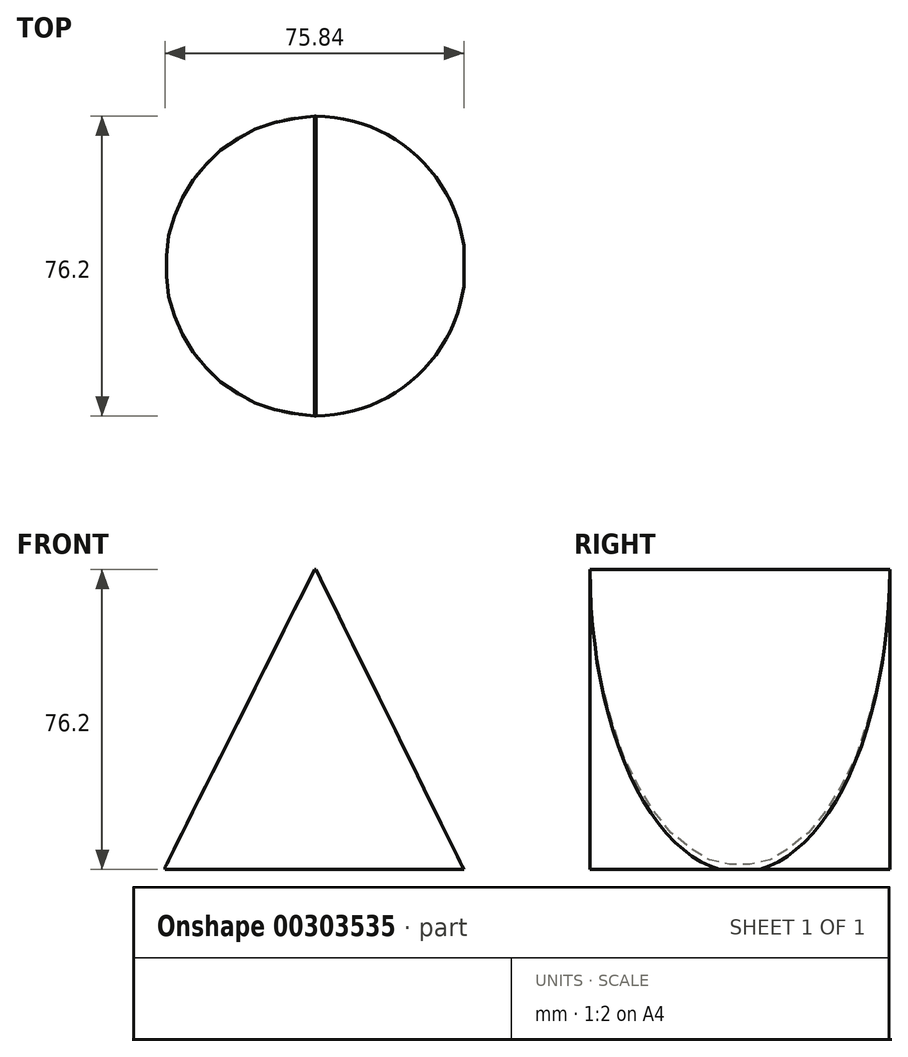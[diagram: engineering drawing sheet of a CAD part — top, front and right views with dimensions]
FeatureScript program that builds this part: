
annotation { "Feature Type Name" : "Feature", "Feature Type Description" : "" }
export const myFeature = defineFeature(function(context is Context, id is Id, definition is map)
    precondition{}
    {
        {
            var Q0;
            Q0=qCreatedBy(makeId("Top.planeOp"),FACE);
            var sketch = newSketch(context, id + "F0", { "sketchPlane" : qUnion([Q0])});
            skCircle(sketch, "E0", {"center": v(0, 0) * mm, "radius": 38.1 * mm});
            skSolve(sketch);
        }
        {
            var Q0;
            Q0 = qSketchRegion(id + "F0", true);
            extrude(context, id + "F1", {"entities" : qUnion([Q0]), "depth" : 76.2 * mm});
        }
        {
            var Q0;
            Q0=qCreatedBy(makeId("Front.planeOp"),FACE);
            var sketch = newSketch(context, id + "F2", { "sketchPlane" : qUnion([Q0])});
            skLineSegment(sketch, "E1", {"start": v(-38.44, 0) * mm, "end": v(0, 76.53) * mm});
            skLineSegment(sketch, "E2", {"start": v(0, 76.53) * mm, "end": v(37.74, 0) * mm});
            skLineSegment(sketch, "E3", {"start": v(37.74, 0) * mm, "end": v(45.74, 0) * mm});
            skLineSegment(sketch, "E4", {"start": v(45.74, 0) * mm, "end": v(45.74, 81.06) * mm});
            skLineSegment(sketch, "E5", {"start": v(45.74, 81.06) * mm, "end": v(-51.66, 81.06) * mm});
            skLineSegment(sketch, "E6", {"start": v(-51.66, 81.06) * mm, "end": v(-49.08, 0) * mm});
            skLineSegment(sketch, "E7", {"start": v(-49.08, 0) * mm, "end": v(-38.44, 0) * mm});
            skSolve(sketch);
        }
        {
            var Q0;
            Q0 = qSketchRegion(id + "F2", true);
            extrude(context, id + "F3", {"entities" : qUnion([Q0]), "operationType" : NewBodyOperationType.REMOVE, "depth" : 71.88 * mm});
        }
        {
            var Q0;
            Q0 = qSketchRegion(id + "F2", true);
            extrude(context, id + "F4", {"entities" : qUnion([Q0]), "operationType" : NewBodyOperationType.REMOVE, "oppositeDirection" : true, "depth" : 64.77 * mm});
        }
    });
